# Revit family: Flush_Valve-Urinal_Concealed-American_Standard-Selectronic-Exposed_Back_Spud-606B3X1_Series
name_source: partatom
category: Plumbing Fixtures
units: mm (PartAtom-declared; Revit-internal decimal feet)

## family parameters
Cut with Voids When Loaded = Yes
Host = Face
OmniClass Number = 23.65.70.00
OmniClass Title = Terminals for Supplied Liquids and Gases
Part Type = Normal
Room Calculation Point = No
Round Connector Dimension = Use Diameter
Shared = Yes

## types (3) — shared parameters
ADA Compliant = Yes
Assembly Code = D2020100
CW Connection = Yes
CWFU = 5
Cold Water Connection Diameter = 1"
Cold Water Connection Radius = 1/2"
Cold Water Connection Width = 4 1/4"
Critical Line Distance from Tube = 6"
Default Elevation = 0"
Description = Ultima Selectronic, Concealed Toilet Flush Valve With Wall Box, Piston-Type, Exposed Back Spud, 1.1 gpf
Finish = Stainless Steel-American Standard-007-Chrome
Finish- Flush Valve = Brass-American Standard-Satin
Flow Requirement = 25 gpm/94.6 L/min
HW Connection = No
Height = 13 7/8"
Installation Type = Exposed Back Spud
Manufacturer = American Standard
Material = Brass-American Standard-Satin
Operating Pressure = 25 psi (flowing) - 80 psi (static)
PK00.CRP Power Kit = No
PK00.HAC Power Kit = No
PK00.MAC Power Kit = No
PK00.PAC Power Kit = No
PK00.WRK Power Kit = No
Price = Prices may vary. Please consult Manufacturer Representative for most up-to-date price list.
Product Documentation Link = https://americanstandard.box.com
Product Page URL = https://www.americanstandard-us.com
Revised Date = 10/01/2021
Type Comments = Power Kits Must Be Purchased Separately.
URL = http://www.americanstandard-us.com
Vent Connection = No
WFU = 5
Warranty Information = 1 Year Limited Warranty
Waste Connection = No
zero-valued in all types: HWFU

## per-type parameters (varying)
| type | Critical Line Distance from Tube Constraint | Flush Rate | NPT Distance to Valve | NPT Distance to Valve Constraint | Tube Length to Fixture | Tube Length to Fixture Constraint |
| 606B.311.007 | 4 1/4" | 1.1 gpf/4.2 Lpf | 4 1/4" | 4 1/4" | 6" | 6" |
| 606B.321.007 | 4 1/4" | 1.28 gpf/4.8 Lpf | 4 1/4" | 4 1/4" | 5" | 5" |
| 606B.361.007 | 5 1/4" | 1.6 gpf/6.0 Lpf | 5 1/4" | 5 1/4" | 10" | 10" |

note: column(s) folded — value = type name in every type: Model

## geometry (parser evidence)
native form markers: Sweep x2
no freeform markers — native parametric forms only
